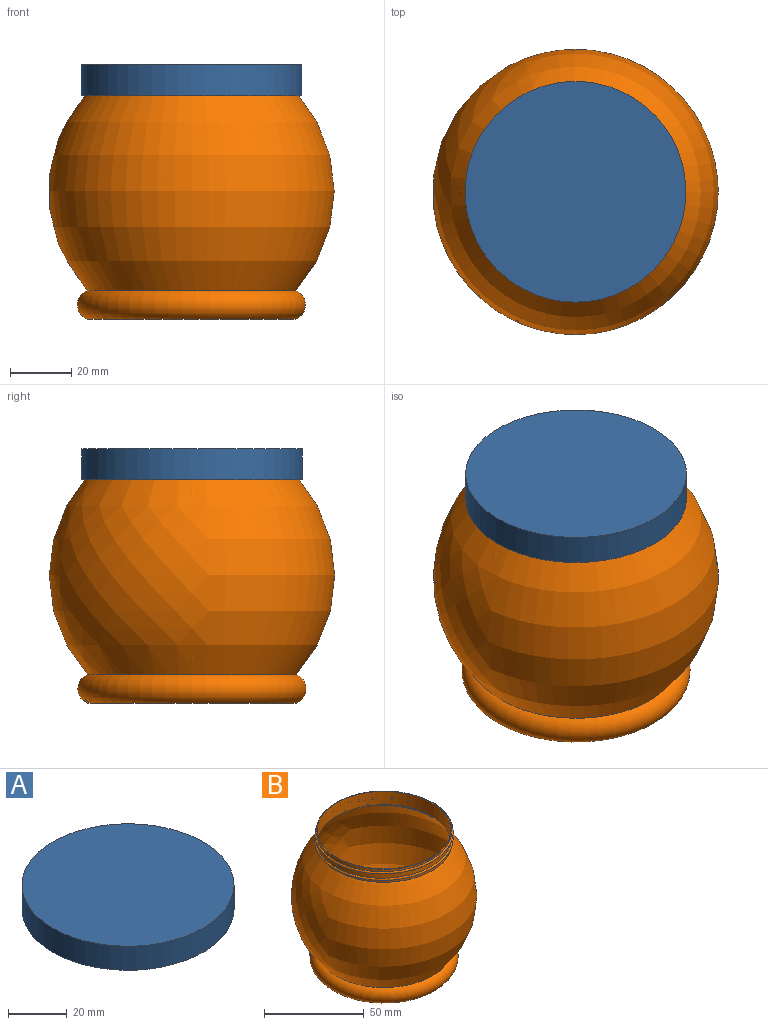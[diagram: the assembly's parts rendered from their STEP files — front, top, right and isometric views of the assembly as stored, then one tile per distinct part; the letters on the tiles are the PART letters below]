
ASSEMBLY  parts=2 mates=1
PART A: 9 faces, bbox 72.6x80.6x11.8 mm
  f0: plane 72.57x72.57mm, normal (0,0,-1), area 405.9mm2, adj f1,f4,f5,f8
  f1: cylinder r=36mm len=72mm, axis (0,0,-1), area 2261.9mm2, adj f0,f2
  f2: plane 72x72mm, normal (0,0,1), area 4071.5mm2, adj f1
  f3: plane 68x68mm, normal (0,0,-1), area 3631.7mm2, adj f6
  f4: cylinder r=34mm len=31.64mm, axis (0,0,-1), area 15.4mm2, adj f0,f5,f8
  f5: cylinder r=34mm len=68mm, axis (0,0,-1), area 482.1mm2, adj f0,f4,f6,f8
  f6: cylinder r=34mm len=68mm, axis (0,0,-1), area 722.4mm2, adj f3,f5,f7,f8
  f7: plane 1.27x0.66mm, normal (0,-1,0), area 0.6mm2, adj f6,f8
  f8: bspline ~79.99x69.27mm, area 789.7mm2, adj f0,f4,f5,f6,f7
PART B: 17 faces, bbox 93.1x93.1x82.1 mm
  f0: plane 68x68mm, normal (0,0,-1), area 3631.7mm2, adj f1
  f1: torus R=32.2mm, axis (0,0,-1), area 2727.4mm2, adj f0,f2
  f2: revolved ~93.03x93.03mm, area 18807mm2, adj f1,f4,f5,f15,f16
  f3: cylinder r=34mm len=68mm, axis (0,0,-1), area 722.4mm2, adj f4,f6,f14,f16
  f4: cylinder r=34mm len=68mm, axis (0,0,-1), area 482.2mm2, adj f2,f3,f5,f16
  f5: cylinder r=34mm len=31.64mm, axis (0,0,-1), area 15.4mm2, adj f2,f4,f16
  f6: plane 68x68mm, normal (0,0,1), area 84.9mm2, adj f3,f10
  f7: plane 67.85x67.85mm, normal (0,0,1), area 3615.5mm2, adj f8
  f8: torus R=32.2mm, axis (0,0,-1), area 2600.1mm2, adj f7,f9
  f9: revolved ~92.25x92.25mm, area 18680.5mm2, adj f8,f10,f11,f12,f13
  f10: cylinder r=33.6mm len=67.2mm, axis (0,0,-1), area 1721.7mm2, adj f6,f9
  f11: bspline ~51.95x39.99mm, area 8.6mm2, adj f9,f12,f13
  f12: cylinder r=33.98mm len=29.59mm, axis (0,0,-1), area 12.1mm2, adj f9,f11,f13
  f13: plane 0.7x0.48mm, normal (0,-1,0), area 0.2mm2, adj f9,f11,f12
  f14: plane 1.27x0.66mm, normal (0,1,0), area 0.6mm2, adj f3,f16
  f15: plane 0.74x0.67mm, normal (0,-1,0), area 0.1mm2, adj f2,f16
  f16: bspline ~79.99x69.27mm, area 825.3mm2, adj f2,f3,f4,f5,f14,f15
PLACE A rot(axis=(0,0,1),90deg) t=(4.11,-3.97,-10.59)mm
PLACE B t=(4.11,-3.97,-9.52)mm fixed
MATE cylindrical A.f1 <-> B.f1  axis (0,0,-1) through (4.11,-3.97,27.41)mm
